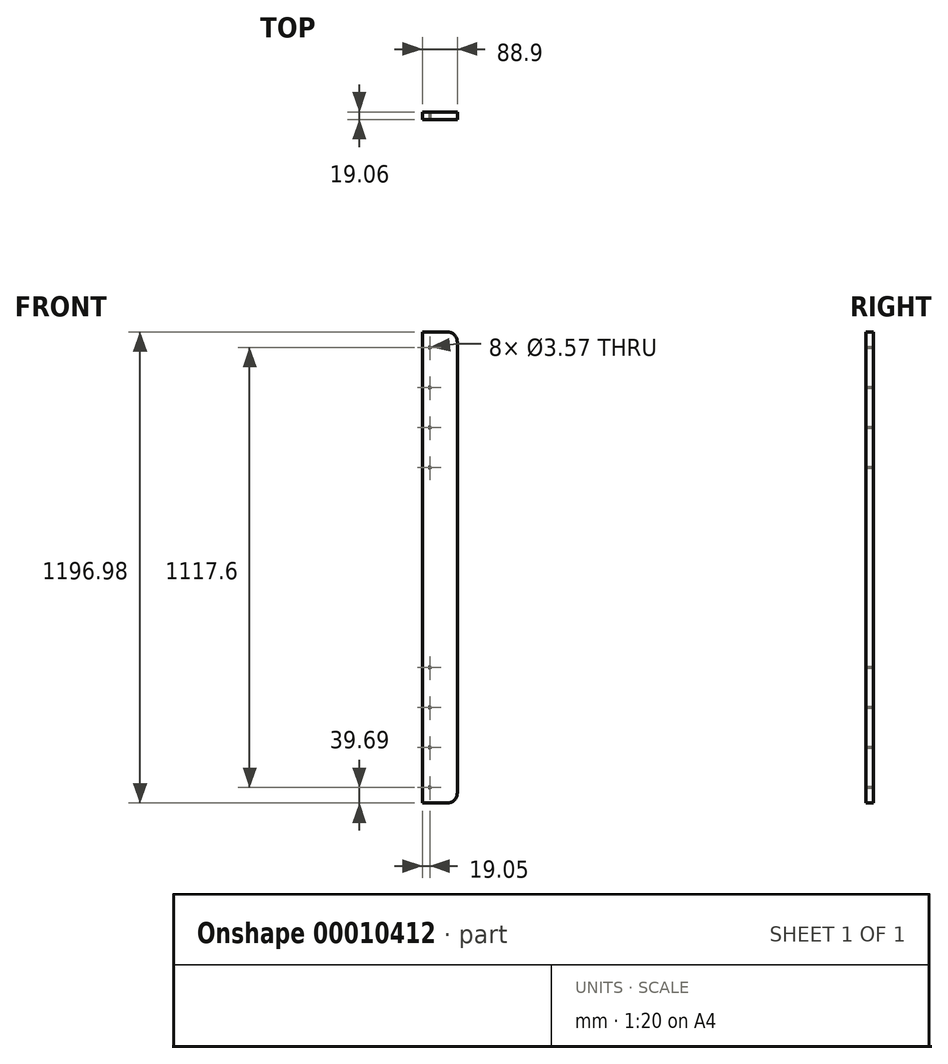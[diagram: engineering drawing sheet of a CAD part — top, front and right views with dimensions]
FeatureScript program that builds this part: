
annotation { "Feature Type Name" : "Feature", "Feature Type Description" : "" }
export const myFeature = defineFeature(function(context is Context, id is Id, definition is map)
    precondition{}
    {
        {
            var Q0;
            Q0=qCreatedBy(makeId("Top.planeOp"),FACE);
            var sketch = newSketch(context, id + "F0", { "sketchPlane" : qUnion([Q0])});
            skLineSegment(sketch, "E0.rect.bottom", {"start": v(44.45, 9.53) * mm, "end": v(-44.45, 9.53) * mm});
            skLineSegment(sketch, "E0.rect.top", {"start": v(44.45, -9.53) * mm, "end": v(-44.45, -9.53) * mm});
            skLineSegment(sketch, "E0.rect.left", {"start": v(44.45, 9.53) * mm, "end": v(44.45, -9.53) * mm});
            skLineSegment(sketch, "E0.rect.right", {"start": v(-44.45, 9.53) * mm, "end": v(-44.45, -9.53) * mm});
            skPoint(sketch, "E0.rect.middle", {"position": v(0, 0) * mm});
            skSolve(sketch);
        }
        {
            var Q0;
            Q0 = qSketchRegion(id + "F0", true);
            extrude(context, id + "F1", {"entities" : qUnion([Q0]), "endBound" : BoundingType.SYMMETRIC, "depth" : 1196.97 * mm});
        }
        {
            var Q0;
            Q0=makeQuery(id+"F1.opExtrude","SWEPT_FACE",FACE,{"disambiguationData":[OSD([sQuery(id+"F0.wireOp",EDGE,"E0.rect.top")])]});
            var sketch = newSketch(context, id + "F2", { "sketchPlane" : qUnion([Q0])});
            skCircle(sketch, "E1", {"center": v(-25.4, -558.8) * mm, "radius": 1.79 * mm});
            skLineSegment(sketch, "E2", {"start": v(44.45, 0) * mm, "end": v(-44.45, 0) * mm, "construction": true});
            skCircle(sketch, "E3.0.1.0", {"center": v(-25.4, -457.2) * mm, "radius": 1.79 * mm});
            skCircle(sketch, "E3.0.2.0", {"center": v(-25.4, -355.6) * mm, "radius": 1.79 * mm});
            skCircle(sketch, "E3.0.3.0", {"center": v(-25.4, -254) * mm, "radius": 1.79 * mm});
            skCircle(sketch, "E4.0.MirrorC", {"center": v(-25.4, 558.8) * mm, "radius": 1.79 * mm});
            skCircle(sketch, "E5.0.MirrorC", {"center": v(-25.4, 457.2) * mm, "radius": 1.79 * mm});
            skCircle(sketch, "E6.0.MirrorC", {"center": v(-25.4, 254) * mm, "radius": 1.79 * mm});
            skCircle(sketch, "E7.2.MirrorC", {"center": v(-25.4, 355.6) * mm, "radius": 1.79 * mm});
            skPoint(sketch, "E8.visualSharp", {"position": v(44.45, -598.49) * mm});
            skSolve(sketch);
        }
        {
            var Q0;
            Q0 = qSketchRegion(id + "F2", true);
            extrude(context, id + "F3", {"entities" : qUnion([Q0]), "operationType" : NewBodyOperationType.REMOVE, "endBound" : BoundingType.THROUGH_ALL, "oppositeDirection" : true, "depth" : 25.4 * mm});
        }
        {
            var Q0;
            Q0=makeQuery(id+"F1.opExtrude","CAP_EDGE",EDGE,{"disambiguationData":[OSD([sQuery(id+"F0.wireOp",EDGE,"E0.rect.left")])],"isStart":true});
            fillet(context, id + "F4", {"entities" : qUnion([Q0]), "radius" : 25.4 * mm, "allowEdgeOverflow" : false});
        }
        {
            var Q0;
            Q0=makeQuery(id+"F1.opExtrude","CAP_EDGE",EDGE,{"disambiguationData":[OSD([sQuery(id+"F0.wireOp",EDGE,"E0.rect.left")])],"isStart":false});
            fillet(context, id + "F5", {"entities" : qUnion([Q0]), "radius" : 25.4 * mm, "tangentPropagation" : true, "allowEdgeOverflow" : false});
        }
    });
